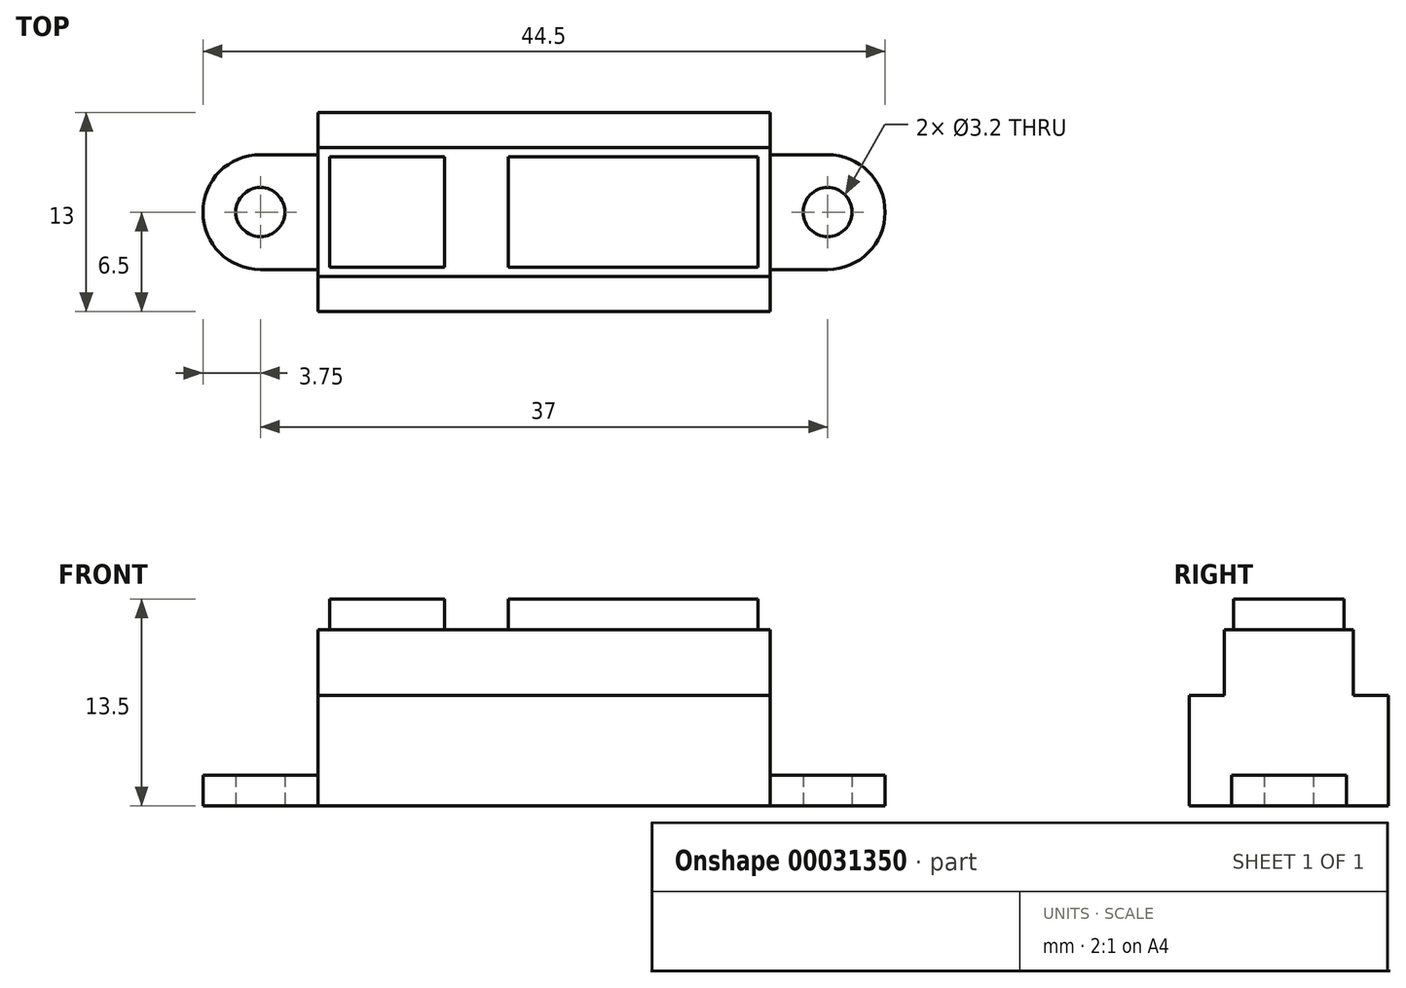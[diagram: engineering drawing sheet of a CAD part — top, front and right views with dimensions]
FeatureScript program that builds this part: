
annotation { "Feature Type Name" : "Feature", "Feature Type Description" : "" }
export const myFeature = defineFeature(function(context is Context, id is Id, definition is map)
    precondition{}
    {
        {
            var Q0;
            Q0=qCreatedBy(makeId("Top.planeOp"),FACE);
            var sketch = newSketch(context, id + "F0", { "sketchPlane" : qUnion([Q0])});
            skLineSegment(sketch, "E0.bottom", {"start": v(-14.75, 6.5) * mm, "end": v(14.75, 6.5) * mm});
            skLineSegment(sketch, "E0.top", {"start": v(-14.75, -6.5) * mm, "end": v(14.75, -6.5) * mm});
            skLineSegment(sketch, "E0.left", {"start": v(-14.75, 6.5) * mm, "end": v(-14.75, -6.5) * mm});
            skLineSegment(sketch, "E0.right", {"start": v(14.75, 6.5) * mm, "end": v(14.75, -6.5) * mm});
            skArc(sketch, "E1", {"start": v(18.5, -3.75) * mm, "mid": v(22.25, 0) * mm, "end": v(18.5, 3.75) * mm});
            skPoint(sketch, "E1.centerSnap0", {"position": v(14.75, 0) * mm});
            skLineSegment(sketch, "E2", {"start": v(14.75, 3.75) * mm, "end": v(18.5, 3.75) * mm});
            skLineSegment(sketch, "E3", {"start": v(14.75, -3.75) * mm, "end": v(18.5, -3.75) * mm});
            skCircle(sketch, "E4", {"center": v(18.5, 0) * mm, "radius": 1.6 * mm});
            skLineSegment(sketch, "E5.MirrorCS", {"start": v(-14.75, 3.75) * mm, "end": v(-18.5, 3.75) * mm});
            skArc(sketch, "E6.MirrorCS", {"start": v(-18.5, -3.75) * mm, "mid": v(-22.25, 0) * mm, "end": v(-18.5, 3.75) * mm});
            skLineSegment(sketch, "E7.MirrorCS", {"start": v(-14.75, -3.75) * mm, "end": v(-18.5, -3.75) * mm});
            skCircle(sketch, "E8.MirrorC", {"center": v(-18.5, 0) * mm, "radius": 1.6 * mm});
            skSolve(sketch);
        }
        {
            var Q0;
            Q0 = qSketchRegion(id + "F0", true);
            extrude(context, id + "F1", {"entities" : qUnion([Q0]), "depth" : 2 * mm});
        }
        {
            var Q0;
            Q0=makeQuery(id+"F1.opExtrude","CAP_FACE",FACE,{"disambiguationData":[OSD([sQuery(id+"F0.wireOp",EDGE,"E0.bottom"),sQuery(id+"F0.wireOp",EDGE,"E0.top"),sQuery(id+"F0.wireOp",EDGE,"E0.left"),sQuery(id+"F0.wireOp",EDGE,"E0.right"),sQuery(id+"F0.wireOp",EDGE,"E1"),sQuery(id+"F0.wireOp",EDGE,"E2"),sQuery(id+"F0.wireOp",EDGE,"E3"),sQuery(id+"F0.wireOp",EDGE,"E4"),sQuery(id+"F0.wireOp",EDGE,"E5.MirrorCS"),sQuery(id+"F0.wireOp",EDGE,"E6.MirrorCS"),sQuery(id+"F0.wireOp",EDGE,"E7.MirrorCS"),sQuery(id+"F0.wireOp",EDGE,"E8.MirrorC")])],"isStart":false});
            var sketch = newSketch(context, id + "F2", { "sketchPlane" : qUnion([Q0])});
            skLineSegment(sketch, "E9.bottom", {"start": v(-14.75, 6.5) * mm, "end": v(14.75, 6.5) * mm});
            skLineSegment(sketch, "E9.top", {"start": v(-14.75, -6.5) * mm, "end": v(14.75, -6.5) * mm});
            skLineSegment(sketch, "E9.left", {"start": v(-14.75, 6.5) * mm, "end": v(-14.75, -6.5) * mm});
            skLineSegment(sketch, "E9.right", {"start": v(14.75, 6.5) * mm, "end": v(14.75, -6.5) * mm});
            skSolve(sketch);
        }
        {
            var Q0;
            Q0 = qSketchRegion(id + "F2", true);
            extrude(context, id + "F3", {"entities" : qUnion([Q0]), "operationType" : NewBodyOperationType.ADD, "depth" : (13.5 - 6.3 - 2) * mm});
        }
        {
            var Q0;
            Q0=makeQuery(id+"F3.opExtrude","CAP_FACE",FACE,{"disambiguationData":[OSD([sQuery(id+"F2.wireOp",EDGE,"E9.bottom"),sQuery(id+"F2.wireOp",EDGE,"E9.top"),sQuery(id+"F2.wireOp",EDGE,"E9.left"),sQuery(id+"F2.wireOp",EDGE,"E9.right")])],"isStart":false});
            var sketch = newSketch(context, id + "F4", { "sketchPlane" : qUnion([Q0])});
            skLineSegment(sketch, "E10.bottom", {"start": v(-14.75, 4.2) * mm, "end": v(14.75, 4.2) * mm});
            skLineSegment(sketch, "E10.top", {"start": v(-14.75, -4.2) * mm, "end": v(14.75, -4.2) * mm});
            skLineSegment(sketch, "E10.left", {"start": v(-14.75, 4.2) * mm, "end": v(-14.75, -4.2) * mm});
            skLineSegment(sketch, "E10.right", {"start": v(14.75, 4.2) * mm, "end": v(14.75, -4.2) * mm});
            skSolve(sketch);
        }
        {
            var Q0;
            Q0 = qSketchRegion(id + "F4", true);
            extrude(context, id + "F5", {"entities" : qUnion([Q0]), "operationType" : NewBodyOperationType.ADD, "depth" : 4.3 * mm});
        }
        {
            var Q0;
            Q0=makeQuery(id+"F5.opExtrude","CAP_FACE",FACE,{"disambiguationData":[OSD([sQuery(id+"F4.wireOp",EDGE,"E10.bottom"),sQuery(id+"F4.wireOp",EDGE,"E10.top"),sQuery(id+"F4.wireOp",EDGE,"E10.left"),sQuery(id+"F4.wireOp",EDGE,"E10.right")])],"isStart":false});
            var sketch = newSketch(context, id + "F6", { "sketchPlane" : qUnion([Q0])});
            skLineSegment(sketch, "E11.bottom", {"start": v(-2.33, 3.6) * mm, "end": v(13.98, 3.6) * mm});
            skLineSegment(sketch, "E11.top", {"start": v(-2.33, -3.6) * mm, "end": v(13.98, -3.6) * mm});
            skLineSegment(sketch, "E11.left", {"start": v(-2.33, 3.6) * mm, "end": v(-2.33, -3.6) * mm});
            skLineSegment(sketch, "E11.right", {"start": v(13.97, 3.6) * mm, "end": v(13.97, -3.6) * mm});
            skLineSegment(sketch, "E12.bottom", {"start": v(-13.98, 3.6) * mm, "end": v(-6.48, 3.6) * mm});
            skLineSegment(sketch, "E12.top", {"start": v(-13.98, -3.6) * mm, "end": v(-6.48, -3.6) * mm});
            skLineSegment(sketch, "E12.left", {"start": v(-13.98, 3.6) * mm, "end": v(-13.98, -3.6) * mm});
            skLineSegment(sketch, "E12.right", {"start": v(-6.48, 3.6) * mm, "end": v(-6.48, -3.6) * mm});
            skSolve(sketch);
        }
        {
            var Q0;
            Q0 = qSketchRegion(id + "F6", true);
            extrude(context, id + "F7", {"entities" : qUnion([Q0]), "operationType" : NewBodyOperationType.ADD, "depth" : 2 * mm});
        }
    });
